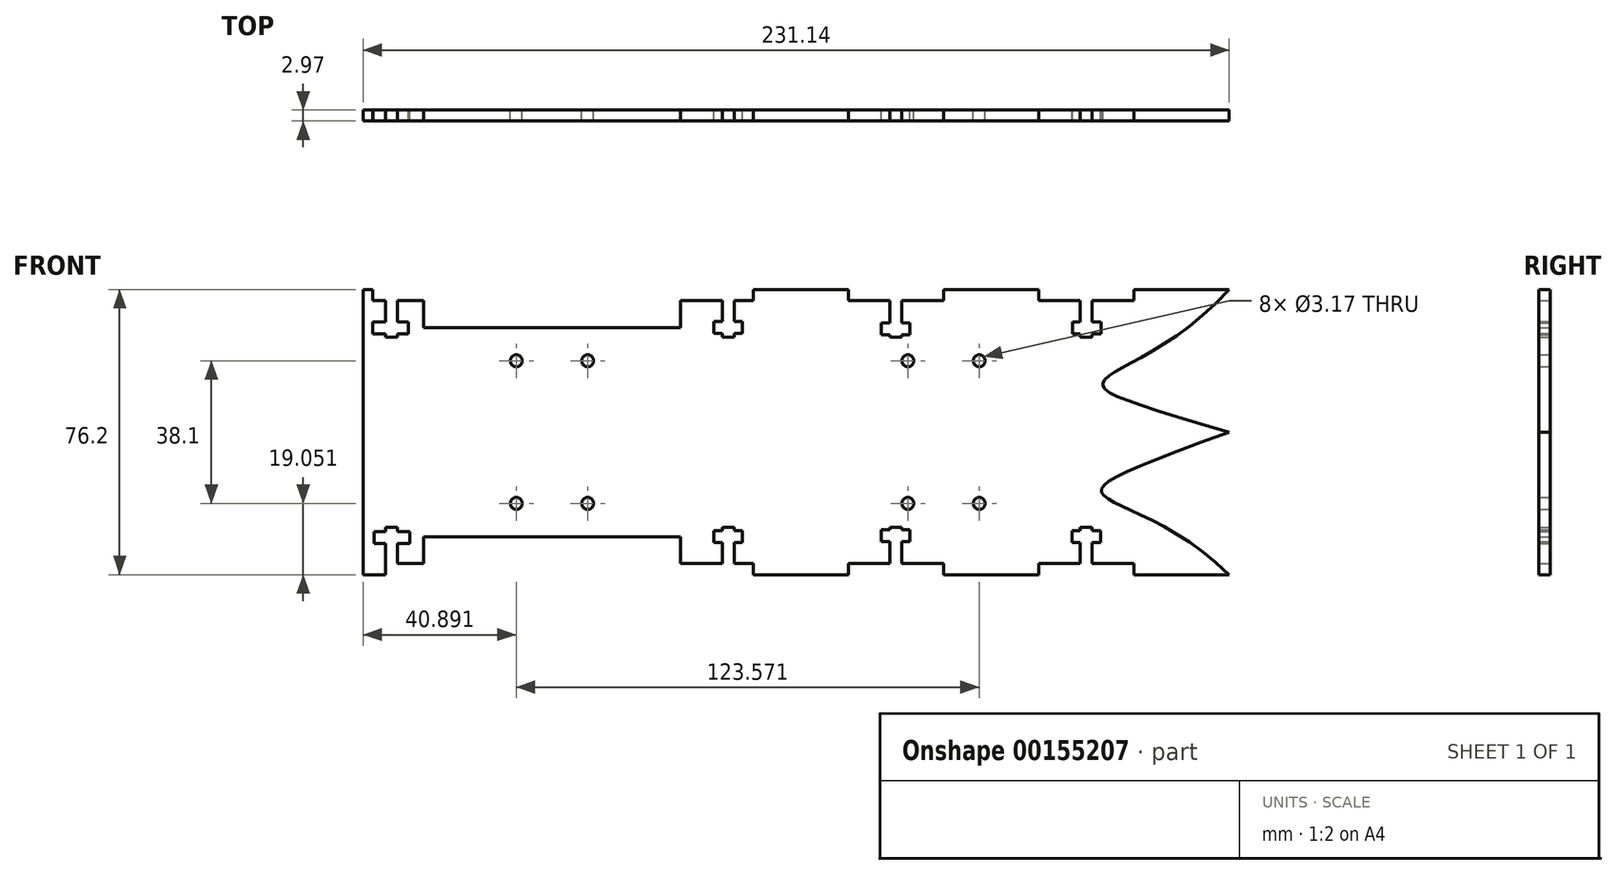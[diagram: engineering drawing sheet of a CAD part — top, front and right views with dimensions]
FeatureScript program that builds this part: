
annotation { "Feature Type Name" : "Feature", "Feature Type Description" : "" }
export const myFeature = defineFeature(function(context is Context, id is Id, definition is map)
    precondition{}
    {
        {
            var Q0;
            Q0=qCreatedBy(makeId("Front.planeOp"),FACE);
            var sketch = newSketch(context, id + "F0", { "sketchPlane" : qUnion([Q0])});
            skLineSegment(sketch, "E0.bottom", {"start": v(-134.13, 54) * mm, "end": v(94.47, 54) * mm});
            skLineSegment(sketch, "E0.top", {"start": v(-134.13, -22.2) * mm, "end": v(94.47, -22.2) * mm});
            skLineSegment(sketch, "E0.left", {"start": v(-134.13, 54) * mm, "end": v(-134.13, -22.2) * mm});
            skLineSegment(sketch, "E1.bottom", {"start": v(69.07, -22.2) * mm, "end": v(43.67, -22.2) * mm});
            skLineSegment(sketch, "E1.top", {"start": v(69.07, -19.23) * mm, "end": v(43.67, -19.23) * mm});
            skLineSegment(sketch, "E1.left", {"start": v(69.07, -22.2) * mm, "end": v(69.07, -19.23) * mm});
            skLineSegment(sketch, "E1.right", {"start": v(43.67, -22.2) * mm, "end": v(43.67, -19.23) * mm});
            skLineSegment(sketch, "E2.bottom", {"start": v(18.27, -22.2) * mm, "end": v(-7.13, -22.2) * mm});
            skLineSegment(sketch, "E2.top", {"start": v(18.27, -19.23) * mm, "end": v(-7.13, -19.23) * mm});
            skLineSegment(sketch, "E2.left", {"start": v(18.27, -22.2) * mm, "end": v(18.27, -19.23) * mm});
            skLineSegment(sketch, "E2.right", {"start": v(-7.13, -22.2) * mm, "end": v(-7.13, -19.23) * mm});
            skLineSegment(sketch, "E3.bottom", {"start": v(-32.53, -22.2) * mm, "end": v(-51.96, -22.2) * mm});
            skLineSegment(sketch, "E3.top", {"start": v(-32.53, -19.23) * mm, "end": v(-51.96, -19.23) * mm});
            skLineSegment(sketch, "E3.left", {"start": v(-32.53, -22.2) * mm, "end": v(-32.53, -19.23) * mm});
            skLineSegment(sketch, "E3.right", {"start": v(-51.96, -22.2) * mm, "end": v(-51.96, -19.23) * mm});
            skLineSegment(sketch, "E4.bottom", {"start": v(-51.96, -22.2) * mm, "end": v(-120.54, -22.2) * mm});
            skLineSegment(sketch, "E4.top", {"start": v(-51.96, -12.04) * mm, "end": v(-120.54, -12.04) * mm});
            skLineSegment(sketch, "E4.left", {"start": v(-51.96, -22.2) * mm, "end": v(-51.96, -12.04) * mm});
            skLineSegment(sketch, "E4.right", {"start": v(-120.54, -22.2) * mm, "end": v(-120.54, -12.04) * mm});
            skLineSegment(sketch, "E5.bottom", {"start": v(69.07, 54) * mm, "end": v(43.67, 54) * mm});
            skLineSegment(sketch, "E5.top", {"start": v(69.07, 51.03) * mm, "end": v(43.67, 51.03) * mm});
            skLineSegment(sketch, "E5.left", {"start": v(69.07, 54) * mm, "end": v(69.07, 51.03) * mm});
            skLineSegment(sketch, "E5.right", {"start": v(43.67, 54) * mm, "end": v(43.67, 51.03) * mm});
            skLineSegment(sketch, "E6.bottom", {"start": v(18.27, 54) * mm, "end": v(-7.13, 54) * mm});
            skLineSegment(sketch, "E7.bottom", {"start": v(-32.53, 54) * mm, "end": v(-51.96, 54) * mm});
            skLineSegment(sketch, "E7.top", {"start": v(-32.53, 51.03) * mm, "end": v(-51.96, 51.03) * mm});
            skLineSegment(sketch, "E7.left", {"start": v(-32.53, 54) * mm, "end": v(-32.53, 51.03) * mm});
            skLineSegment(sketch, "E7.right", {"start": v(-51.96, 54) * mm, "end": v(-51.96, 51.03) * mm});
            skLineSegment(sketch, "E8.bottom", {"start": v(-51.96, 54) * mm, "end": v(-120.54, 54) * mm});
            skLineSegment(sketch, "E8.top", {"start": v(-51.96, 43.84) * mm, "end": v(-120.54, 43.84) * mm});
            skLineSegment(sketch, "E8.left", {"start": v(-51.96, 54) * mm, "end": v(-51.96, 43.84) * mm});
            skLineSegment(sketch, "E8.right", {"start": v(-120.54, 54) * mm, "end": v(-120.54, 43.84) * mm});
            skFitSpline(sketch, "E9", {"points": [v(94.47, 54) * mm, v(94.47, 15.9) * mm], "startDerivative": vector(-79.84, -89.28) * mm, "endDerivative": vector(180.96, -53.28) * mm});
            skFitSpline(sketch, "E10", {"points": [v(94.47, 15.9) * mm, v(94.47, -22.2) * mm], "startDerivative": vector(-183.14, -67.48) * mm, "endDerivative": vector(79.78, -80.54) * mm});
            skLineSegment(sketch, "E11.top", {"start": v(3.98, -19.23) * mm, "end": v(7.16, -19.23) * mm});
            skLineSegment(sketch, "E12.MirrorCS", {"start": v(9.37, 54) * mm, "end": v(12.54, 54) * mm});
            skLineSegment(sketch, "E13.MirrorCS", {"start": v(9.37, 53.98) * mm, "end": v(12.54, 54) * mm});
            skLineSegment(sketch, "E14.MirrorCS", {"start": v(9.33, 53.98) * mm, "end": v(12.57, 53.98) * mm});
            skLineSegment(sketch, "E15.MirrorCS", {"start": v(60.03, 53.88) * mm, "end": v(62.97, 53.79) * mm});
            skLineSegment(sketch, "E16.bottom", {"start": v(-41.1, 54) * mm, "end": v(-44.28, 54) * mm});
            skLineSegment(sketch, "E17", {"start": v(-134.13, 51.03) * mm, "end": v(-120.54, 51.03) * mm});
            skLineSegment(sketch, "E18.bottom", {"start": v(-130.64, 54) * mm, "end": v(-127.46, 54) * mm});
            skLineSegment(sketch, "E18.top", {"start": v(-130.64, 41.3) * mm, "end": v(-127.46, 41.3) * mm});
            skLineSegment(sketch, "E18.left", {"start": v(-130.64, 54) * mm, "end": v(-130.64, 41.3) * mm});
            skLineSegment(sketch, "E18.right", {"start": v(-127.46, 54) * mm, "end": v(-127.46, 41.3) * mm});
            skLineSegment(sketch, "E19.MirrorCS", {"start": v(-124.57, 42.18) * mm, "end": v(-124.57, 45.35) * mm});
            skLineSegment(sketch, "E20.MirrorCS", {"start": v(-134.1, 42.18) * mm, "end": v(-134.1, 45.35) * mm});
            skLineSegment(sketch, "E21.MirrorCS", {"start": v(-134.1, 45.35) * mm, "end": v(-124.57, 45.35) * mm});
            skLineSegment(sketch, "E22.MirrorCS", {"start": v(-134.1, 42.18) * mm, "end": v(-124.57, 42.18) * mm});
            skLineSegment(sketch, "E23.bottom", {"start": v(-127.46, -22.2) * mm, "end": v(-130.64, -22.2) * mm});
            skLineSegment(sketch, "E23.top", {"start": v(-127.46, -9.5) * mm, "end": v(-130.64, -9.5) * mm});
            skLineSegment(sketch, "E23.left", {"start": v(-127.46, -22.2) * mm, "end": v(-127.46, -9.5) * mm});
            skLineSegment(sketch, "E23.right", {"start": v(-130.64, -22.2) * mm, "end": v(-130.64, -9.5) * mm});
            skLineSegment(sketch, "E24.MirrorCS", {"start": v(-133.68, -10.69) * mm, "end": v(-124.16, -10.69) * mm});
            skLineSegment(sketch, "E25.MirrorCS", {"start": v(-133.68, -13.86) * mm, "end": v(-124.16, -13.86) * mm});
            skLineSegment(sketch, "E26.MirrorCS", {"start": v(-133.68, -13.86) * mm, "end": v(-133.68, -10.69) * mm});
            skLineSegment(sketch, "E27", {"start": v(-124.16, -10.69) * mm, "end": v(-124.16, -13.86) * mm});
            skLineSegment(sketch, "E28.bottom", {"start": v(-134.13, 54) * mm, "end": v(-136.67, 54) * mm});
            skLineSegment(sketch, "E28.top", {"start": v(-134.13, -22.2) * mm, "end": v(-136.67, -22.2) * mm});
            skLineSegment(sketch, "E28.right", {"start": v(-136.67, 54) * mm, "end": v(-136.67, -22.2) * mm});
            skLineSegment(sketch, "E29.bottom", {"start": v(-120.54, -22.2) * mm, "end": v(-134.13, -22.2) * mm});
            skLineSegment(sketch, "E29.top", {"start": v(-120.54, -19.23) * mm, "end": v(-134.13, -19.23) * mm});
            skLineSegment(sketch, "E29.left", {"start": v(-120.54, -22.2) * mm, "end": v(-120.54, -19.23) * mm});
            skLineSegment(sketch, "E29.right", {"start": v(-134.13, -22.2) * mm, "end": v(-134.13, -19.23) * mm});
            skLineSegment(sketch, "E30.bottom", {"start": v(-7.13, 54) * mm, "end": v(18.27, 54) * mm});
            skLineSegment(sketch, "E30.top", {"start": v(-7.13, 51.03) * mm, "end": v(18.27, 51.03) * mm});
            skLineSegment(sketch, "E30.left", {"start": v(-7.13, 54) * mm, "end": v(-7.13, 51.03) * mm});
            skLineSegment(sketch, "E30.right", {"start": v(18.27, 54) * mm, "end": v(18.27, 51.03) * mm});
            skLineSegment(sketch, "E31.bottom", {"start": v(57.96, -22.2) * mm, "end": v(54.78, -22.2) * mm});
            skLineSegment(sketch, "E31.top", {"start": v(57.96, -9.5) * mm, "end": v(54.78, -9.5) * mm});
            skLineSegment(sketch, "E31.left", {"start": v(57.96, -22.2) * mm, "end": v(57.96, -9.5) * mm});
            skLineSegment(sketch, "E31.right", {"start": v(54.78, -22.2) * mm, "end": v(54.78, -9.5) * mm});
            skLineSegment(sketch, "E32.bottom", {"start": v(52.62, -10.37) * mm, "end": v(60.24, -10.37) * mm});
            skLineSegment(sketch, "E32.top", {"start": v(52.62, -13.55) * mm, "end": v(60.24, -13.55) * mm});
            skLineSegment(sketch, "E32.left", {"start": v(52.62, -10.37) * mm, "end": v(52.62, -13.55) * mm});
            skLineSegment(sketch, "E32.right", {"start": v(60.24, -10.37) * mm, "end": v(60.24, -13.55) * mm});
            skLineSegment(sketch, "E33.bottom", {"start": v(10.05, -32.3) * mm, "end": v(17.67, -32.3) * mm});
            skLineSegment(sketch, "E33.top", {"start": v(10.05, -35.48) * mm, "end": v(17.67, -35.48) * mm});
            skLineSegment(sketch, "E33.left", {"start": v(10.05, -32.3) * mm, "end": v(10.05, -35.48) * mm});
            skLineSegment(sketch, "E33.right", {"start": v(17.67, -32.3) * mm, "end": v(17.67, -35.48) * mm});
            skLineSegment(sketch, "E34.bottom", {"start": v(7.16, -22.2) * mm, "end": v(3.98, -22.2) * mm});
            skLineSegment(sketch, "E34.top", {"start": v(7.16, -9.5) * mm, "end": v(3.98, -9.5) * mm});
            skLineSegment(sketch, "E34.left", {"start": v(7.16, -22.2) * mm, "end": v(7.16, -9.5) * mm});
            skLineSegment(sketch, "E34.right", {"start": v(3.98, -22.2) * mm, "end": v(3.98, -9.5) * mm});
            skLineSegment(sketch, "E35.bottom", {"start": v(1.7, -10.23) * mm, "end": v(9.31, -10.23) * mm});
            skLineSegment(sketch, "E35.top", {"start": v(1.7, -13.4) * mm, "end": v(9.31, -13.4) * mm});
            skLineSegment(sketch, "E35.left", {"start": v(1.7, -10.23) * mm, "end": v(1.7, -13.4) * mm});
            skLineSegment(sketch, "E35.right", {"start": v(9.31, -10.23) * mm, "end": v(9.31, -13.4) * mm});
            skLineSegment(sketch, "E36.bottom", {"start": v(-37.61, -22.2) * mm, "end": v(-40.79, -22.2) * mm});
            skLineSegment(sketch, "E36.top", {"start": v(-37.61, -9.5) * mm, "end": v(-40.79, -9.5) * mm});
            skLineSegment(sketch, "E36.left", {"start": v(-37.61, -22.2) * mm, "end": v(-37.61, -9.5) * mm});
            skLineSegment(sketch, "E36.right", {"start": v(-40.79, -22.2) * mm, "end": v(-40.79, -9.5) * mm});
            skLineSegment(sketch, "E37.bottom", {"start": v(-43.03, -10.48) * mm, "end": v(-35.41, -10.48) * mm});
            skLineSegment(sketch, "E37.top", {"start": v(-43.03, -13.65) * mm, "end": v(-35.41, -13.65) * mm});
            skLineSegment(sketch, "E37.left", {"start": v(-43.03, -10.48) * mm, "end": v(-43.03, -13.65) * mm});
            skLineSegment(sketch, "E37.right", {"start": v(-35.41, -10.48) * mm, "end": v(-35.41, -13.65) * mm});
            skLineSegment(sketch, "E38.bottom", {"start": v(54.78, 54) * mm, "end": v(57.96, 54) * mm});
            skLineSegment(sketch, "E38.top", {"start": v(54.78, 41.3) * mm, "end": v(57.96, 41.3) * mm});
            skLineSegment(sketch, "E38.left", {"start": v(54.78, 54) * mm, "end": v(54.78, 41.3) * mm});
            skLineSegment(sketch, "E38.right", {"start": v(57.96, 54) * mm, "end": v(57.96, 41.3) * mm});
            skLineSegment(sketch, "E39.bottom", {"start": v(52.7, 45.26) * mm, "end": v(60.32, 45.26) * mm});
            skLineSegment(sketch, "E39.top", {"start": v(52.7, 42.09) * mm, "end": v(60.32, 42.09) * mm});
            skLineSegment(sketch, "E39.left", {"start": v(52.7, 45.26) * mm, "end": v(52.7, 42.09) * mm});
            skLineSegment(sketch, "E39.right", {"start": v(60.32, 45.26) * mm, "end": v(60.32, 42.09) * mm});
            skLineSegment(sketch, "E40.bottom", {"start": v(3.98, 54) * mm, "end": v(7.16, 54) * mm});
            skLineSegment(sketch, "E40.top", {"start": v(3.98, 41.3) * mm, "end": v(7.16, 41.3) * mm});
            skLineSegment(sketch, "E40.left", {"start": v(3.98, 54) * mm, "end": v(3.98, 41.3) * mm});
            skLineSegment(sketch, "E40.right", {"start": v(7.16, 54) * mm, "end": v(7.16, 41.3) * mm});
            skLineSegment(sketch, "E41.bottom", {"start": v(1.68, 45.12) * mm, "end": v(9.3, 45.12) * mm});
            skLineSegment(sketch, "E41.top", {"start": v(1.68, 41.94) * mm, "end": v(9.3, 41.94) * mm});
            skLineSegment(sketch, "E41.left", {"start": v(1.68, 45.12) * mm, "end": v(1.68, 41.94) * mm});
            skLineSegment(sketch, "E41.right", {"start": v(9.3, 45.12) * mm, "end": v(9.3, 41.94) * mm});
            skLineSegment(sketch, "E42.bottom", {"start": v(-37.61, 54) * mm, "end": v(-40.79, 54) * mm});
            skLineSegment(sketch, "E42.top", {"start": v(-37.61, 41.3) * mm, "end": v(-40.79, 41.3) * mm});
            skLineSegment(sketch, "E42.left", {"start": v(-37.61, 54) * mm, "end": v(-37.61, 41.3) * mm});
            skLineSegment(sketch, "E42.right", {"start": v(-40.79, 54) * mm, "end": v(-40.79, 41.3) * mm});
            skLineSegment(sketch, "E43.bottom", {"start": v(-43, 45.4) * mm, "end": v(-35.38, 45.4) * mm});
            skLineSegment(sketch, "E43.top", {"start": v(-43, 42.23) * mm, "end": v(-35.38, 42.23) * mm});
            skLineSegment(sketch, "E43.left", {"start": v(-43, 45.4) * mm, "end": v(-43, 42.23) * mm});
            skLineSegment(sketch, "E43.right", {"start": v(-35.38, 45.4) * mm, "end": v(-35.38, 42.23) * mm});
            skLineSegment(sketch, "E44", {"start": v(-108.73, 28.6) * mm, "end": v(52.16, 28.6) * mm});
            skLineSegment(sketch, "E45", {"start": v(-108.73, 3.2) * mm, "end": v(50.37, 3.2) * mm});
            skLineSegment(sketch, "E46", {"start": v(-108.73, 3.2) * mm, "end": v(-108.73, 28.6) * mm});
            skLineSegment(sketch, "E47", {"start": v(50.37, 3.2) * mm, "end": v(50.37, 28.6) * mm});
            skLineSegment(sketch, "E48", {"start": v(8.74, -3.15) * mm, "end": v(27.8, -3.15) * mm});
            skCircle(sketch, "E49", {"center": v(27.8, -3.15) * mm, "radius": 1.59 * mm});
            skLineSegment(sketch, "E50", {"start": v(8.74, 34.95) * mm, "end": v(27.8, 34.95) * mm});
            skCircle(sketch, "E51", {"center": v(8.74, -3.15) * mm, "radius": 1.59 * mm});
            skCircle(sketch, "E52", {"center": v(27.8, 34.95) * mm, "radius": 1.59 * mm});
            skCircle(sketch, "E53", {"center": v(8.74, 34.95) * mm, "radius": 1.59 * mm});
            skLineSegment(sketch, "E54", {"start": v(-95.78, -3.15) * mm, "end": v(-76.73, -3.15) * mm});
            skCircle(sketch, "E55", {"center": v(-95.78, -3.15) * mm, "radius": 1.59 * mm});
            skCircle(sketch, "E56", {"center": v(-76.73, -3.15) * mm, "radius": 1.59 * mm});
            skLineSegment(sketch, "E57", {"start": v(-95.78, 34.95) * mm, "end": v(-76.73, 34.95) * mm});
            skCircle(sketch, "E58", {"center": v(-76.73, 34.95) * mm, "radius": 1.59 * mm});
            skCircle(sketch, "E59", {"center": v(-95.78, 34.95) * mm, "radius": 1.59 * mm});
            skSolve(sketch);
        }
        {
            var Q0;
            {var subQ0=sQuery(id+"F0.wireOp",EDGE,"E0.left");var subQ1=sQuery(id+"F0.wireOp",EDGE,"E0.top");var subQ2=makeQuery(id+"F0.imprint","INTERSECT",VERTEX,{"derivedFrom":[subQ1,subQ0]});Q0=makeQuery(id+"F0.imprint","IMPRINT",FACE,{"disambiguationData":[TD([[makeQuery(id+"F0.imprint","IMPRINT",EDGE,{"disambiguationData":[TD([[subQ2,1.0]])],"derivedFrom":subQ0}),1.0]])]});}
            var Q1;
            {var subQ0=sQuery(id+"F0.wireOp",EDGE,"E17");var subQ1=sQuery(id+"F0.wireOp",EDGE,"E0.left");var subQ2=makeQuery(id+"F0.imprint","INTERSECT",VERTEX,{"derivedFrom":[subQ1,subQ0]});Q1=makeQuery(id+"F0.imprint","IMPRINT",FACE,{"disambiguationData":[TD([[makeQuery(id+"F0.imprint","IMPRINT",EDGE,{"disambiguationData":[TD([[subQ2,-1.0]])],"derivedFrom":subQ1}),1.0]])]});}
            var Q2;
            Q2=makeQuery(id+"F0.imprint","IMPRINT",FACE,{"disambiguationData":[TD([[makeQuery(id+"F0.imprint","IMPRINT",EDGE,{"derivedFrom":sQuery(id+"F0.wireOp",EDGE,"E1.top")}),-1.0]])]});
            var Q3;
            {var subQ0=sQuery(id+"F0.wireOp",EDGE,"E5.left");Q3=makeQuery(id+"F0.imprint","IMPRINT",FACE,{"disambiguationData":[TD([[makeQuery(id+"F0.imprint","IMPRINT",EDGE,{"derivedFrom":subQ0}),1.0]])]});}
            var Q4;
            {var subQ11=sQuery(id+"F0.wireOp",EDGE,"6b61488c-ecd6-439c-897c-79aafdacd241.MirrorCS");Q4=makeQuery(id+"F0.imprint","IMPRINT",FACE,{"disambiguationData":[TD([[makeQuery(id+"F0.imprint","IMPRINT",EDGE,{"derivedFrom":subQ11}),1.0]])]});}
            var Q5;
            {var subQ0=sQuery(id+"F0.wireOp",EDGE,"E0.left");var subQ1=sQuery(id+"F0.wireOp",EDGE,"E17");var subQ2=makeQuery(id+"F0.imprint","INTERSECT",VERTEX,{"derivedFrom":[subQ1,subQ0]});Q5=makeQuery(id+"F0.imprint","IMPRINT",FACE,{"disambiguationData":[TD([[makeQuery(id+"F0.imprint","IMPRINT",EDGE,{"disambiguationData":[TD([[subQ2,-1.0]])],"derivedFrom":subQ1}),-1.0]])]});}
            var Q6;
            {var subQ3=sQuery(id+"F0.wireOp",EDGE,"E23.right");var subQ5=sQuery(id+"F0.wireOp",EDGE,"E25.MirrorCS");var subQ6=makeQuery(id+"F0.imprint","INTERSECT",VERTEX,{"derivedFrom":[subQ3,subQ5]});Q6=makeQuery(id+"F0.imprint","IMPRINT",FACE,{"disambiguationData":[TD([[makeQuery(id+"F0.imprint","IMPRINT",EDGE,{"disambiguationData":[TD([[subQ6,1.0]])],"derivedFrom":subQ5}),-1.0]])]});}
            var Q7;
            {var subQ3=sQuery(id+"F0.wireOp",EDGE,"E28.bottom");Q7=makeQuery(id+"F0.imprint","IMPRINT",FACE,{"disambiguationData":[TD([[makeQuery(id+"F0.imprint","IMPRINT",EDGE,{"derivedFrom":subQ3}),1.0]])]});}
            var Q8;
            Q8=makeQuery(id+"F0.imprint","IMPRINT",FACE,{"disambiguationData":[TD([[makeQuery(id+"F0.imprint","IMPRINT",EDGE,{"derivedFrom":sQuery(id+"F0.wireOp",EDGE,"E45")}),1.0]])]});
            extrude(context, id + "F1", {"entities" : qUnion([Q0, Q1, Q2, Q3, Q4, Q5, Q6, Q7, Q8]), "depth" : 2.97 * mm});
        }
    });
